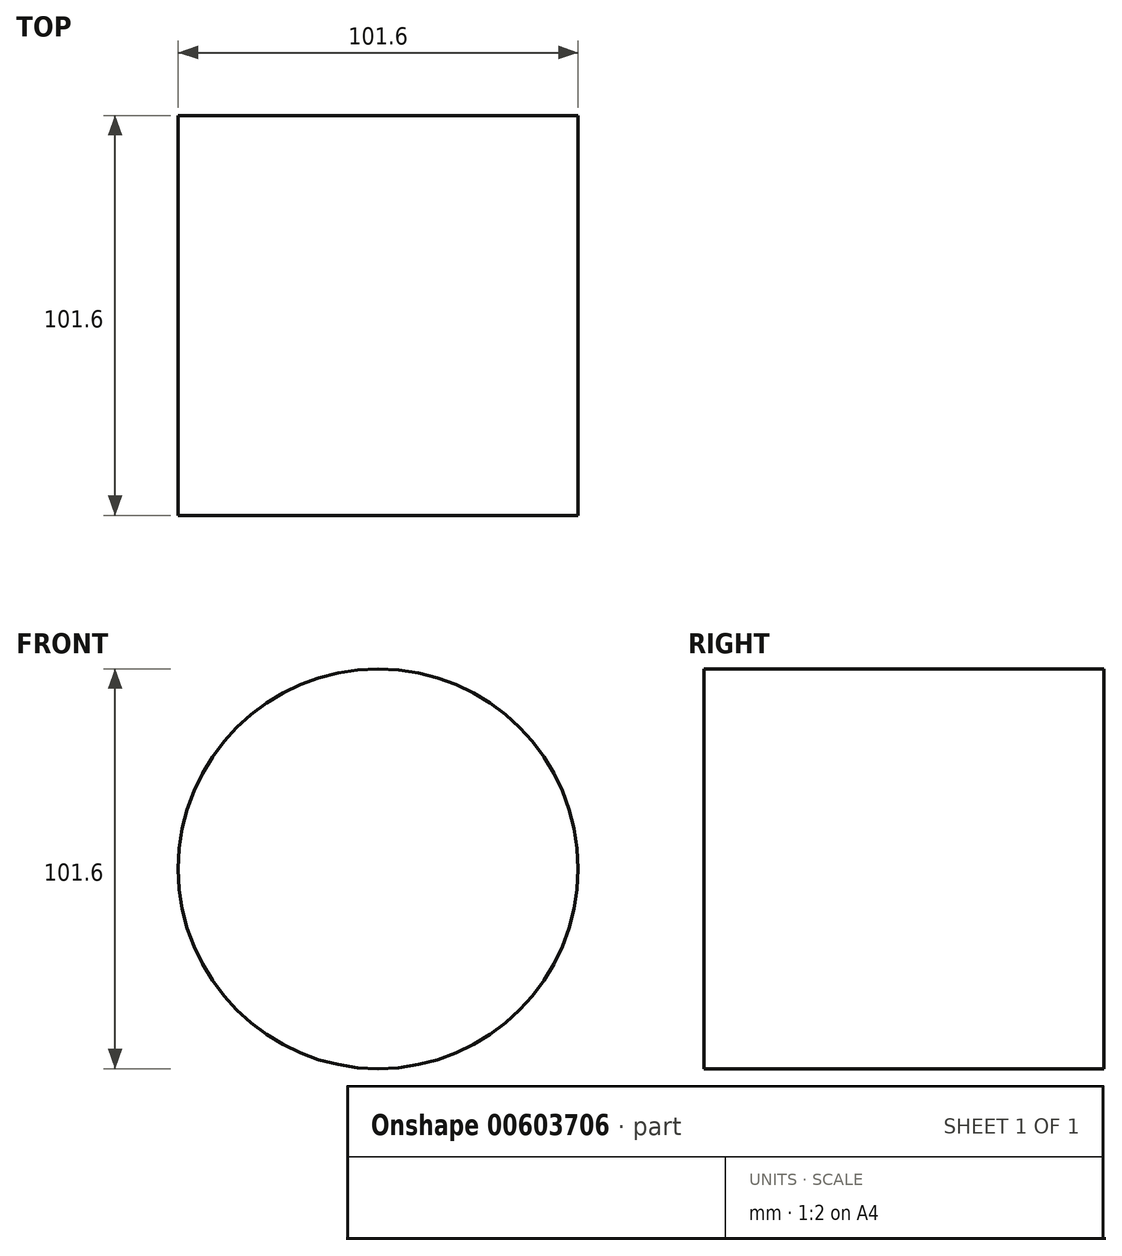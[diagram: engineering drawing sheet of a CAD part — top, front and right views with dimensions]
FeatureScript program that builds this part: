
annotation { "Feature Type Name" : "Feature", "Feature Type Description" : "" }
export const myFeature = defineFeature(function(context is Context, id is Id, definition is map)
    precondition{}
    {
        {
            var Q0;
            Q0=qCreatedBy(makeId("Front.planeOp"),FACE);
            var sketch = newSketch(context, id + "F0", { "sketchPlane" : qUnion([Q0])});
            skCircle(sketch, "E0", {"center": v(0, 0) * mm, "radius": 50.8 * mm});
            skSolve(sketch);
        }
        {
            var Q0;
            Q0=makeQuery(id+"F0.imprint","IMPRINT",FACE,{"disambiguationData":[TD([[makeQuery(id+"F0.imprint","IMPRINT",EDGE,{"derivedFrom":sQuery(id+"F0.wireOp",EDGE,"E0")}),1.0]])]});
            extrude(context, id + "F1", {"entities" : qUnion([Q0]), "endBound" : BoundingType.SYMMETRIC, "depth" : 101.6 * mm, "offsetDistance" : 25.4 * mm});
        }
    });
